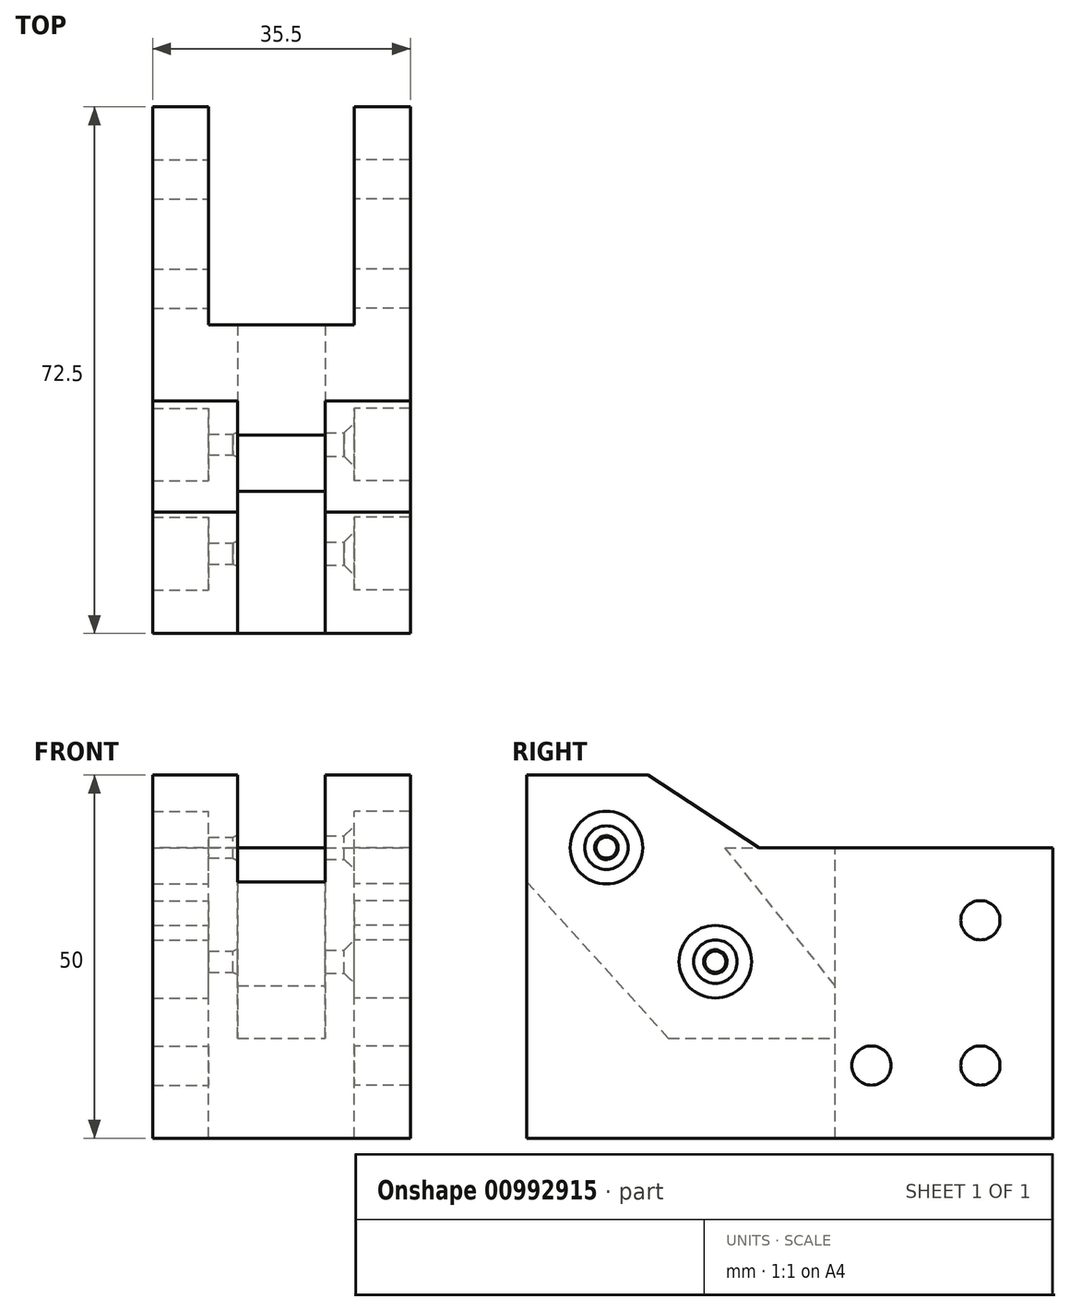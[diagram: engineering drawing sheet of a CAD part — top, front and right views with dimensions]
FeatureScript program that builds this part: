
annotation { "Feature Type Name" : "Feature", "Feature Type Description" : "" }
export const myFeature = defineFeature(function(context is Context, id is Id, definition is map)
    precondition{}
    {
        {
            var Q0;
            Q0=qCreatedBy(makeId("Right.planeOp"),FACE);
            var sketch = newSketch(context, id + "F0", { "sketchPlane" : qUnion([Q0])});
            skLineSegment(sketch, "E0", {"start": v(-62.1, 10.14) * mm, "end": v(10.4, 10.14) * mm});
            skLineSegment(sketch, "E1", {"start": v(10.4, 10.14) * mm, "end": v(10.4, 50.14) * mm});
            skLineSegment(sketch, "E2", {"start": v(-62.1, 50.14) * mm, "end": v(-62.1, 10.14) * mm});
            skLineSegment(sketch, "E3.top", {"start": v(-62.1, 60.14) * mm, "end": v(-30.1, 60.14) * mm});
            skLineSegment(sketch, "E3.left", {"start": v(-62.1, 50.14) * mm, "end": v(-62.1, 60.14) * mm});
            skLineSegment(sketch, "E3.right", {"start": v(-30.1, 50.14) * mm, "end": v(-30.1, 60.14) * mm});
            skLineSegment(sketch, "E4", {"start": v(-30.1, 50.14) * mm, "end": v(10.4, 50.14) * mm});
            skLineSegment(sketch, "E5", {"start": v(-62.1, 50.14) * mm, "end": v(-51.1, 50.14) * mm, "construction": true});
            skLineSegment(sketch, "E6", {"start": v(-51.1, 50.14) * mm, "end": v(-51.1, 34.44) * mm, "construction": true});
            skLineSegment(sketch, "E7", {"start": v(-51.1, 34.44) * mm, "end": v(-31.1, 34.44) * mm, "construction": true});
            skLineSegment(sketch, "E8", {"start": v(10.4, 10.14) * mm, "end": v(10.4, 20.14) * mm, "construction": true});
            skLineSegment(sketch, "E9", {"start": v(10.4, 20.14) * mm, "end": v(0.4, 20.14) * mm, "construction": true});
            skLineSegment(sketch, "E10", {"start": v(0.4, 20.14) * mm, "end": v(-14.6, 20.14) * mm, "construction": true});
            skLineSegment(sketch, "E11", {"start": v(0.4, 20.14) * mm, "end": v(0.4, 40.14) * mm, "construction": true});
            skSolve(sketch);
        }
        {
            var Q0;
            Q0=qCreatedBy(makeId("Front.planeOp"),FACE);
            var sketch = newSketch(context, id + "F1", { "sketchPlane" : qUnion([Q0])});
            skLineSegment(sketch, "E12", {"start": v(0, 10.14) * mm, "end": v(-20.1, 10.14) * mm});
            skLineSegment(sketch, "E13", {"start": v(-20.1, 50.14) * mm, "end": v(0, 50.14) * mm});
            skLineSegment(sketch, "E14", {"start": v(0, 50.14) * mm, "end": v(0, 10.14) * mm});
            skLineSegment(sketch, "E15", {"start": v(-20.1, 50.14) * mm, "end": v(-20.1, 40.14) * mm, "construction": true});
            skLineSegment(sketch, "E16", {"start": v(-20.1, 40.14) * mm, "end": v(-20.1, 20.14) * mm, "construction": true});
            skLineSegment(sketch, "E17", {"start": v(-20.1, 43.24) * mm, "end": v(-20.1, 37.04) * mm, "construction": true});
            skLineSegment(sketch, "E18", {"start": v(-20.1, 40.14) * mm, "end": v(-14, 40.14) * mm, "construction": true});
            skLineSegment(sketch, "E19", {"start": v(-20.1, 20.14) * mm, "end": v(-14, 20.14) * mm, "construction": true});
            skSolve(sketch);
        }
        {
            var Q0;
            Q0=qCreatedBy(makeId("Right.planeOp"),FACE);
            var sketch = newSketch(context, id + "F2", { "sketchPlane" : qUnion([Q0])});
            skLineSegment(sketch, "E20", {"start": v(-19.6, 10.14) * mm, "end": v(-19.6, 50.14) * mm});
            skLineSegment(sketch, "E21.0", {"start": v(-51.1, 34.44) * mm, "end": v(-31.1, 34.44) * mm, "construction": true});
            skPoint(sketch, "E22", {"position": v(-36.1, 34.44) * mm});
            skLineSegment(sketch, "E23.0", {"start": v(-62.1, 50.14) * mm, "end": v(-51.1, 50.14) * mm, "construction": true});
            skLineSegment(sketch, "E24.0", {"start": v(-62.1, 50.14) * mm, "end": v(-62.1, 10.14) * mm});
            skLineSegment(sketch, "E25.0", {"start": v(-62.1, 50.14) * mm, "end": v(-62.1, 60.14) * mm});
            skLineSegment(sketch, "E26", {"start": v(-62.1, 60.14) * mm, "end": v(-45.38, 60.14) * mm});
            skLineSegment(sketch, "E27", {"start": v(-45.38, 60.14) * mm, "end": v(-30.1, 50.14) * mm});
            skCircle(sketch, "E28", {"center": v(-51.1, 50.14) * mm, "radius": 9 * mm, "construction": true});
            skCircle(sketch, "E29", {"center": v(-36.1, 34.44) * mm, "radius": 9 * mm, "construction": true});
            skLineSegment(sketch, "E30", {"start": v(-30.1, 50.14) * mm, "end": v(-19.6, 50.14) * mm});
            skLineSegment(sketch, "E31", {"start": v(-62.1, 10.14) * mm, "end": v(-19.6, 10.14) * mm});
            skPoint(sketch, "E32.0", {"position": v(10.4, 10.14) * mm});
            skPoint(sketch, "E33.0", {"position": v(10.4, 50.14) * mm});
            skLineSegment(sketch, "E34", {"start": v(-19.6, 50.14) * mm, "end": v(10.4, 50.14) * mm});
            skLineSegment(sketch, "E35", {"start": v(10.4, 10.14) * mm, "end": v(-19.6, 10.14) * mm});
            skLineSegment(sketch, "E36", {"start": v(10.4, 50.14) * mm, "end": v(10.4, 10.14) * mm});
            skCircle(sketch, "E37", {"center": v(-51.1, 50.14) * mm, "radius": 5 * mm});
            skCircle(sketch, "E38", {"center": v(-36.1, 34.44) * mm, "radius": 5 * mm});
            skSolve(sketch);
        }
        {
            var Q0;
            {var subQ1=sQuery(id+"F2.wireOp",EDGE,"E24.0");Q0=makeQuery(id+"F2.imprint","IMPRINT",FACE,{"disambiguationData":[TD([[makeQuery(id+"F2.imprint","IMPRINT",EDGE,{"derivedFrom":subQ1}),1.0]])]});}
            var Q1;
            {var subQ0=sQuery(id+"F2.wireOp",EDGE,"E20");Q1=makeQuery(id+"F2.imprint","IMPRINT",FACE,{"disambiguationData":[TD([[makeQuery(id+"F2.imprint","IMPRINT",EDGE,{"derivedFrom":subQ0}),1.0]])]});}
            var Q2;
            Q2=makeQuery(id+"F2.imprint","IMPRINT",FACE,{"disambiguationData":[TD([[makeQuery(id+"F2.imprint","IMPRINT",EDGE,{"derivedFrom":sQuery(id+"F2.wireOp",EDGE,"E37")}),1.0]])]});
            var Q3;
            Q3=makeQuery(id+"F2.imprint","IMPRINT",FACE,{"disambiguationData":[TD([[makeQuery(id+"F2.imprint","IMPRINT",EDGE,{"derivedFrom":sQuery(id+"F2.wireOp",EDGE,"E38")}),1.0]])]});
            extrude(context, id + "F3", {"entities" : qUnion([Q0, Q1, Q2, Q3]), "oppositeDirection" : true, "depth" : 4 * mm, "offsetDistance" : 25 * mm});
        }
        {
            var Q0;
            Q0=makeQuery(id+"F2.imprint","IMPRINT",FACE,{"disambiguationData":[TD([[makeQuery(id+"F2.imprint","IMPRINT",EDGE,{"derivedFrom":sQuery(id+"F2.wireOp",EDGE,"E20")}),-1.0]])]});
            var Q1;
            {var subQ0=sQuery(id+"F2.wireOp",EDGE,"E20");Q1=makeQuery(id+"F2.imprint","IMPRINT",FACE,{"disambiguationData":[TD([[makeQuery(id+"F2.imprint","IMPRINT",EDGE,{"derivedFrom":subQ0}),1.0]])]});}
            extrude(context, id + "F4", {"entities" : qUnion([Q0, Q1]), "operationType" : NewBodyOperationType.ADD, "depth" : 7.7 * mm, "offsetDistance" : 25 * mm});
        }
        {
            var Q0;
            Q0=sQuery(id+"F0.wireOp",VERTEX,"E11.end");
            var Q1;
            Q1=sQuery(id+"F0.wireOp",VERTEX,"E9.end");
            var Q2;
            Q2=sQuery(id+"F0.wireOp",VERTEX,"E10.end");
            var Q3;
            Q3=makeQuery(id+"F3.opExtrude","SWEPT_BODY",BODY,{"disambiguationData":[OSD([sQuery(id+"F2.wireOp",EDGE,"E20"),sQuery(id+"F2.wireOp",EDGE,"E24.0"),sQuery(id+"F2.wireOp",EDGE,"E25.0"),sQuery(id+"F2.wireOp",EDGE,"E27"),sQuery(id+"F2.wireOp",EDGE,"E26"),sQuery(id+"F2.wireOp",EDGE,"E30"),sQuery(id+"F2.wireOp",EDGE,"E31")])]});
            hole(context, id + "F5", {"style" : HoleStyle.SIMPLE, "endStyle" : HoleEndStyle.THROUGH, "oppositeDirection" : true, "holeDiameter" : 5.4 * mm, "majorDiameter" : 5 * mm, "isTappedThrough" : true, "tappedDepth" : 12 * mm, "tapClearance" : 3, "locations" : qUnion([Q0, Q1, Q2]), "scope" : qUnion([Q3])});
        }
        {
            var Q0;
            Q0=sQuery(id+"F1.wireOp",EDGE,"E13");
            cPoint(context, id + "F6", {"entities" : qUnion([Q0]), "parameter" : 0.5});
        }
        {
            var Q0;
            Q0=qCreatedBy(makeId("Right.planeOp"),FACE);
            var Q1;
            Q1 = qCreatedBy(id + "F6" ,VERTEX);
            cPlane(context, id + "F7", {"entities" : qUnion([Q0, Q1]), "cplaneType" : CPlaneType.PLANE_POINT, "offset" : 25 * mm, "width" : 150 * mm, "height" : 150 * mm});
        }
        {
            var Q0;
            Q0=makeQuery(id+"F3.opExtrude","SWEPT_BODY",BODY,{"disambiguationData":[OSD([sQuery(id+"F2.wireOp",EDGE,"E20"),sQuery(id+"F2.wireOp",EDGE,"E24.0"),sQuery(id+"F2.wireOp",EDGE,"E25.0"),sQuery(id+"F2.wireOp",EDGE,"E27"),sQuery(id+"F2.wireOp",EDGE,"E26"),sQuery(id+"F2.wireOp",EDGE,"E30"),sQuery(id+"F2.wireOp",EDGE,"E31")])]});
            var Q1;
            Q1=qCreatedBy(id+"F7.planeOp",FACE);
            mirror(context, id + "F8", {"entities" : qUnion([Q0]), "mirrorPlane" : qUnion([Q1])});
        }
        {
            var Q0;
            Q0=sQuery(id+"F2.wireOp",VERTEX,"E23.0.end");
            var Q1;
            Q1=sQuery(id+"F2.wireOp",VERTEX,"E22");
            var Q2;
            Q2=makeQuery(id+"F3.opExtrude","SWEPT_BODY",BODY,{"disambiguationData":[OSD([sQuery(id+"F2.wireOp",EDGE,"E20"),sQuery(id+"F2.wireOp",EDGE,"E24.0"),sQuery(id+"F2.wireOp",EDGE,"E25.0"),sQuery(id+"F2.wireOp",EDGE,"E27"),sQuery(id+"F2.wireOp",EDGE,"E26"),sQuery(id+"F2.wireOp",EDGE,"E30"),sQuery(id+"F2.wireOp",EDGE,"E31")])]});
            hole(context, id + "F9", {"style" : HoleStyle.C_SINK, "endStyle" : HoleEndStyle.THROUGH, "holeDiameter" : 3.2 * mm, "cSinkDiameter" : 6 * mm, "cSinkAngle" : 90 * degree, "majorDiameter" : 5 * mm, "isTappedThrough" : true, "tappedDepth" : 12 * mm, "tapClearance" : 3, "locations" : qUnion([Q0, Q1]), "scope" : qUnion([Q2])});
        }
        {
            var Q0;
            Q0=makeQuery(id+"F8.opPattern","COPY",FACE,{"derivedFrom":makeQuery(id+"F3.opExtrude","CAP_FACE",FACE,{"disambiguationData":[OSD([sQuery(id+"F2.wireOp",EDGE,"E20"),sQuery(id+"F2.wireOp",EDGE,"E24.0"),sQuery(id+"F2.wireOp",EDGE,"E25.0"),sQuery(id+"F2.wireOp",EDGE,"E27"),sQuery(id+"F2.wireOp",EDGE,"E26"),sQuery(id+"F2.wireOp",EDGE,"E30"),sQuery(id+"F2.wireOp",EDGE,"E31")])],"isStart":false}),"instanceName":"1"});
            var sketch = newSketch(context, id + "F10", { "sketchPlane" : qUnion([Q0])});
            skPoint(sketch, "E39", {"position": v(-36.1, 34.44) * mm});
            skPoint(sketch, "E40.0", {"position": v(-51.1, 50.14) * mm});
            skSolve(sketch);
        }
        {
            var Q0;
            Q0=sQuery(id+"F10.wireOp",VERTEX,"E39");
            var Q1;
            Q1=sQuery(id+"F10.wireOp",VERTEX,"E40.0");
            var Q2;
            Q2=makeQuery(id+"F8.opPattern","COPY",BODY,{"derivedFrom":makeQuery(id+"F3.opExtrude","SWEPT_BODY",BODY,{"disambiguationData":[OSD([sQuery(id+"F2.wireOp",EDGE,"E20"),sQuery(id+"F2.wireOp",EDGE,"E24.0"),sQuery(id+"F2.wireOp",EDGE,"E25.0"),sQuery(id+"F2.wireOp",EDGE,"E27"),sQuery(id+"F2.wireOp",EDGE,"E26"),sQuery(id+"F2.wireOp",EDGE,"E30"),sQuery(id+"F2.wireOp",EDGE,"E31")])]}),"instanceName":"1"});
            hole(context, id + "F11", {"style" : HoleStyle.C_SINK, "endStyle" : HoleEndStyle.THROUGH, "holeDiameter" : 2.9 * mm, "cSinkDiameter" : 3.5 * mm, "cSinkAngle" : 50 * degree, "majorDiameter" : 5 * mm, "isTappedThrough" : true, "tappedDepth" : 12 * mm, "tapClearance" : 3, "locations" : qUnion([Q0, Q1]), "scope" : qUnion([Q2])});
        }
        {
            var Q0;
            Q0=makeQuery(id+"F3.opExtrude","CAP_FACE",FACE,{"disambiguationData":[OSD([sQuery(id+"F2.wireOp",EDGE,"E20"),sQuery(id+"F2.wireOp",EDGE,"E24.0"),sQuery(id+"F2.wireOp",EDGE,"E25.0"),sQuery(id+"F2.wireOp",EDGE,"E27"),sQuery(id+"F2.wireOp",EDGE,"E26"),sQuery(id+"F2.wireOp",EDGE,"E30"),sQuery(id+"F2.wireOp",EDGE,"E31")])],"isStart":false});
            var sketch = newSketch(context, id + "F12", { "sketchPlane" : qUnion([Q0])});
            skLineSegment(sketch, "E41", {"start": v(62.1, 45.44) * mm, "end": v(42.57, 23.91) * mm});
            skLineSegment(sketch, "E42", {"start": v(42.57, 23.91) * mm, "end": v(42.57, 10.14) * mm});
            skLineSegment(sketch, "E43", {"start": v(42.57, 10.14) * mm, "end": v(62.1, 10.14) * mm});
            skLineSegment(sketch, "E44", {"start": v(62.1, 10.14) * mm, "end": v(62.1, 45.44) * mm});
            skLineSegment(sketch, "E45", {"start": v(19.6, 31.13) * mm, "end": v(34.78, 50.14) * mm});
            skLineSegment(sketch, "E46", {"start": v(34.78, 50.14) * mm, "end": v(30.1, 50.14) * mm});
            skLineSegment(sketch, "E47", {"start": v(30.1, 50.14) * mm, "end": v(19.6, 50.14) * mm});
            skLineSegment(sketch, "E48", {"start": v(19.6, 50.14) * mm, "end": v(19.6, 31.13) * mm});
            skLineSegment(sketch, "E49.bottom", {"start": v(42.57, 23.91) * mm, "end": v(19.6, 23.91) * mm});
            skLineSegment(sketch, "E49.top", {"start": v(42.57, 10.14) * mm, "end": v(19.6, 10.14) * mm});
            skLineSegment(sketch, "E49.right", {"start": v(19.6, 23.91) * mm, "end": v(19.6, 10.14) * mm});
            skSolve(sketch);
        }
        {
            var Q0;
            Q0 = qSketchRegion(id + "F12", true);
            extrude(context, id + "F13", {"entities" : qUnion([Q0]), "operationType" : NewBodyOperationType.ADD, "endBound" : BoundingType.UP_TO_NEXT, "depth" : 25 * mm, "offsetDistance" : 25 * mm});
        }
    });
